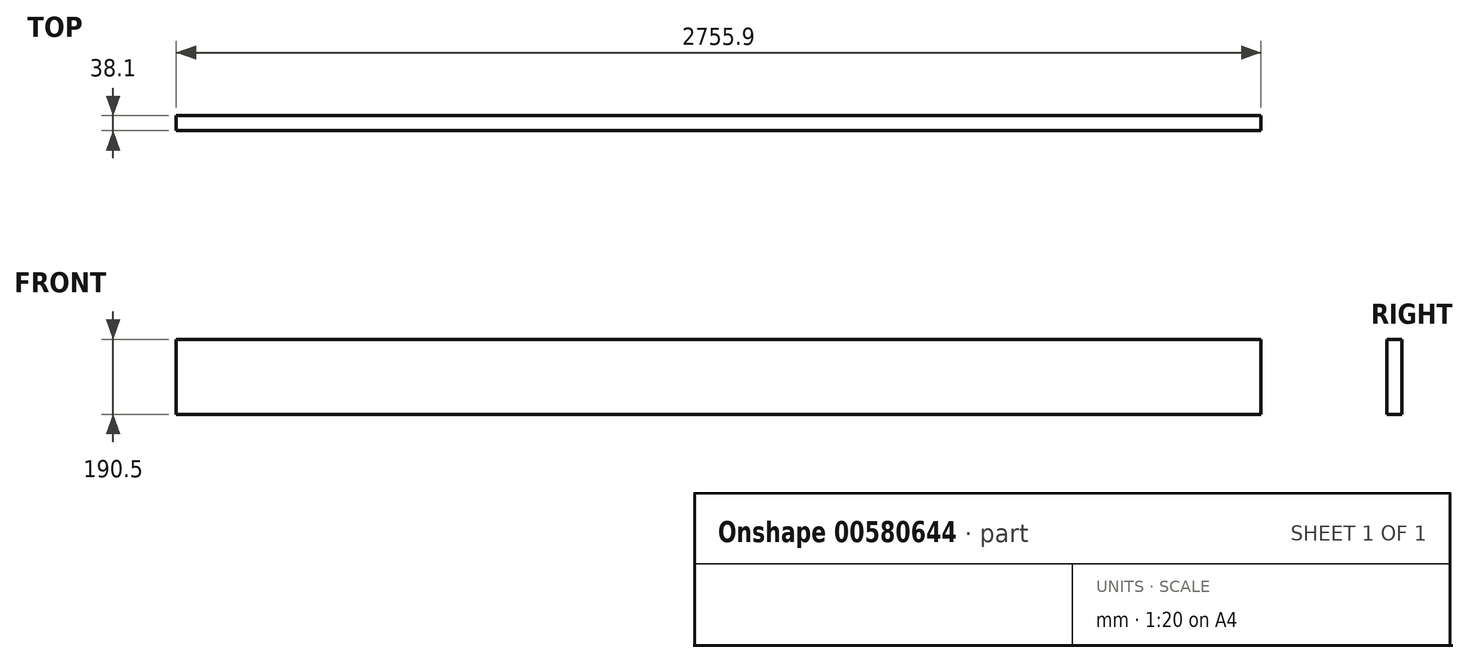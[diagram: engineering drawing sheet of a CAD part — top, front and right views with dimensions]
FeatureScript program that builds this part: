
annotation { "Feature Type Name" : "Feature", "Feature Type Description" : "" }
export const myFeature = defineFeature(function(context is Context, id is Id, definition is map)
    precondition{}
    {
        {
            var Q0;
            Q0=qCreatedBy(makeId("Top.planeOp"),FACE);
            var sketch = newSketch(context, id + "F0", { "sketchPlane" : qUnion([Q0])});
            skLineSegment(sketch, "E0.bottom", {"start": v(1377.95, -19.05) * mm, "end": v(-1377.95, -19.05) * mm});
            skLineSegment(sketch, "E0.top", {"start": v(1377.95, 19.05) * mm, "end": v(-1377.95, 19.05) * mm});
            skLineSegment(sketch, "E0.left", {"start": v(1377.95, -19.05) * mm, "end": v(1377.95, 19.05) * mm});
            skLineSegment(sketch, "E0.right", {"start": v(-1377.95, -19.05) * mm, "end": v(-1377.95, 19.05) * mm});
            skPoint(sketch, "E0.middle", {"position": v(0, 0) * mm});
            skSolve(sketch);
        }
        {
            var Q0;
            Q0=makeQuery(id+"F0.imprint","IMPRINT",FACE,{"disambiguationData":[TD([[makeQuery(id+"F0.imprint","IMPRINT",EDGE,{"derivedFrom":sQuery(id+"F0.wireOp",EDGE,"E0.bottom")}),-1.0]])]});
            extrude(context, id + "F1", {"entities" : qUnion([Q0]), "depth" : 190.5 * mm, "offsetDistance" : 25.4 * mm});
        }
    });
